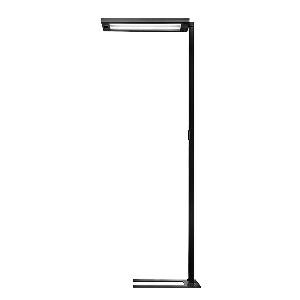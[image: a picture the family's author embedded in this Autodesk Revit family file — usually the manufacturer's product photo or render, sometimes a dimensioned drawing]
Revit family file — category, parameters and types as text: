
# Revit family: lavigo_-_dps_14000_840_r_g2_00807385_9b14
name_source: partatom
category: Lighting Fixtures
units: mm (PartAtom-declared; Revit-internal decimal feet)

## family parameters
Cut with Voids When Loaded = No
Host = Face
Light Source = No
Part Type = Normal
Room Calculation Point = No
Round Connector Dimension = Use Diameter
Shared = No

## types (1)
- LAVIGO - DPS 14000/840/R/G2 (1 x LED, 14050 lm, 4000K)
    Apparent Load = 93 VA
    Approval mark = CE
    CIE Flux Codes = 60 87 97 12 100
    Color Rendering = 80-89
    Color Temperature = 4000K
    Control Gear = Electronic ballast
    Default Elevation = 1800 mm
    Description = DPS 14000/840/R/G2|Free-standing luminaire|light source: LED|work equipment: Electronic ballast|connected load: 220-240 V, 50/60 Hz|Power consumption: approx. 93 W|standby: approx. 0,50|power factor: approx. 0,943|luminous flux: 14050 lm|luminous efficacy: 151 lm/W|light distribution: Direct/indirect|direct ratio: approx. 12 %|colour temperature: Cold white, ca. 4000 K|color rendering index (CRI): >= 80|chromaticity tolerance:  3 SDCM|technology: Presence and daylight sensor control (PIR)|operation: Multi-function switch|luminaire body|material: Steel/plastic|surface: Painted|colour: Black|lamp cover: Acrylic (PMMA), Satine|tubular section|material: Steel tube|surface: Painted|Form: Tubular section upright|colour of tubular section: Black|luminaire base|Form: C-form flat|weight (net): approx. 19.7 kg|mains lead: 3.00 m Mains plug CEE 7/VII|Fastening: Floor standing base|decorative contrast side parts: Black|glare control: Prism aperture|luminance(L65): <= 3000 cd/m|unified glare rating(4H 8H): <=  16|special features: Luminaire head detachable, Cradle to Cradle Certified TM, Direct light component with edge light and light-guide technology for homogenous light exit, Flicker-free, Integrated light and presence sensor PIR, Retrofittable with TALK module, Separated, direct and indirect light individually adjustable|
    Frequency = 50 Hz, 60 Hz
    Height = 36 mm
    Lamp = 1 x LED
    Lamp Light Flux = 14050 lm
    Lamp count = 1
    Length = 675 mm
    Luminous efficacy = 151 lm/W
    Manufacturer = Waldmann
    ModVariant = No
    Model = 00807385
    Mounting Place = Floor
    Mounting Type = Freestanding
    Number of Poles = 1
    OnlyDefault = Yes
    Power Factor = 1
    Product Name = LAVIGO - DPS 14000/840/R/G2
    Product group = Free standing luminaire
    ProductGroupID = 13
    Protection Class = Protection class I
    Protection Degree = IP 20
    RLX_Detail_Level = 1
    RLX_Emergency_Light_Flux = 0 lm
    RLX_Emergency_Type = 0
    RLX_Emergency_Type_DB = No
    RlxData = <blob elided: 38033 chars, md5=18e22d1b>
    Socket = socket
    Standby Power = 0 W
    System Light Flux = 14050 lm
    System Power = 93 W
    Type Comments = Product without accessories
    Type Image = 121771000-00807385.jpg
    URL = http://relux.com
    VarID = ---
    Voltage = 230 V
    Voltage Range = 220-240 V
    Weight = 0.00 kg
    Width = 320 mm

## geometry (parser evidence)
native form markers: Blend x4, Sweep x15
no freeform markers — native parametric forms only
